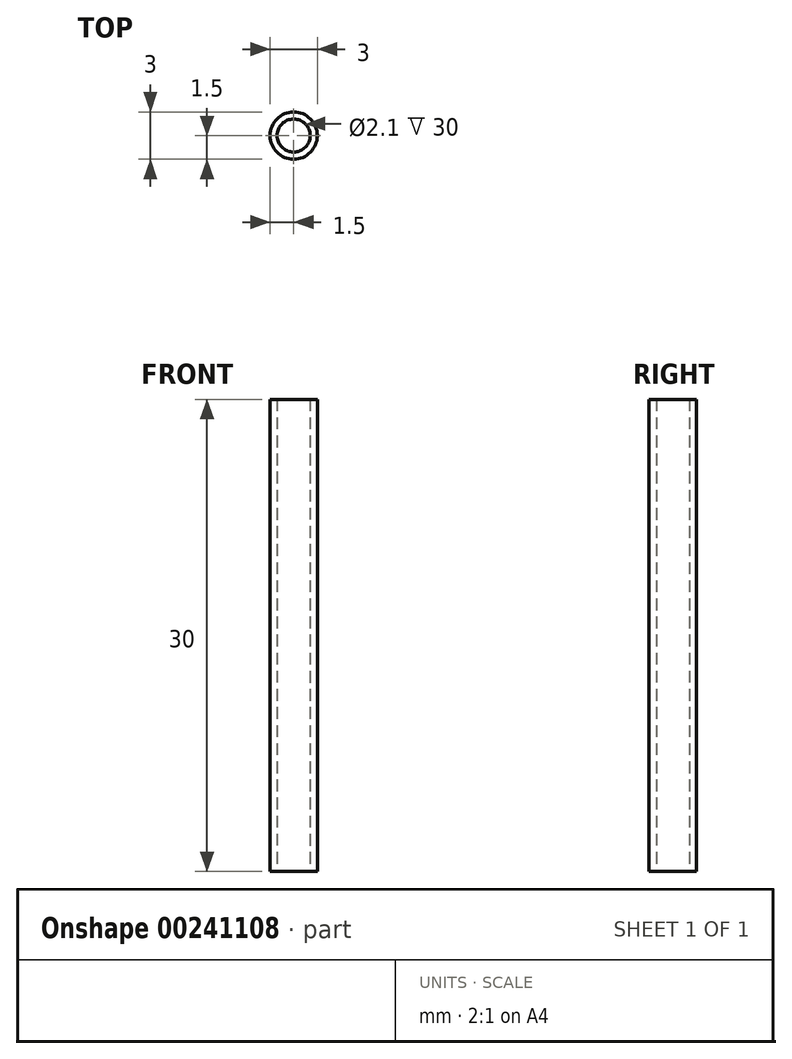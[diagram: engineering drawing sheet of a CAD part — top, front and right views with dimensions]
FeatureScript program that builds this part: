
annotation { "Feature Type Name" : "Feature", "Feature Type Description" : "" }
export const myFeature = defineFeature(function(context is Context, id is Id, definition is map)
    precondition{}
    {
        {
            var Q0;
            Q0=qCreatedBy(makeId("Top.planeOp"),FACE);
            var sketch = newSketch(context, id + "F0", { "sketchPlane" : qUnion([Q0])});
            skCircle(sketch, "E0", {"center": v(0, 0) * mm, "radius": 1.5 * mm});
            skCircle(sketch, "E1", {"center": v(0, 0) * mm, "radius": 1.05 * mm});
            skSolve(sketch);
        }
        {
            var Q0;
            Q0 = qSketchRegion(id + "F0", true);
            extrude(context, id + "F1", {"entities" : qUnion([Q0]), "depth" : 30 * mm});
        }
    });
